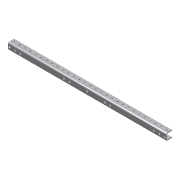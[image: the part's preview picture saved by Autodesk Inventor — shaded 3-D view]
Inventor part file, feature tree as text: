
AUTODESK INVENTOR PART (.ipt)
format: ipt  version: 2013 (Build 170138000, 138)  size: 232,960 bytes
history: native  units: in
note: dims shown in document units (in); Inventor stores cm internally (conversion verified against a paired STEP export)
features: projected_geometry x8, extrude x3, sketch x3, other x1, mirror x1, imported_body x1
ambient origin geometry x8: Origin, YZ Plane, XZ Plane, XY Plane, X Axis, Y Axis, Z Axis, Center Point
feature tree (17):
  other  "Short C Channel for drive1"
  extrude  "Extrusion1"  TaperAngle=0.0deg  [1 undecoded]
  extrude  "Extrusion2"  Depth=0.15in
  extrude  "Extrusion3"  Depth=1.0in TaperAngle=0.0deg
  mirror  "Mirror1"
  imported_body  "Base1"
  sketch  "Sketch1"  dims[d1=0.0in d3=0.0in]
  projected_geometry  "Projected Loop1"
  projected_geometry  "Projected Loop2"
  projected_geometry  "Projected Loop3"
  projected_geometry  "Projected Loop4"
  sketch  "Sketch2"  dims[d4=0.38in d5=0.15in]
  projected_geometry  "Projected Loop5"
  projected_geometry  "Projected Loop6"
  projected_geometry  "Projected Loop7"
  projected_geometry  "Projected Loop8"
  sketch  "Sketch3"  dims[d6=12.25in d7=1.0in d8=0.0in]
note: 1 required parameter value undecoded (feature->parameter linkage not recoverable at this tier; creation-order binding heuristic only, values carry confidence <= 0.55)
